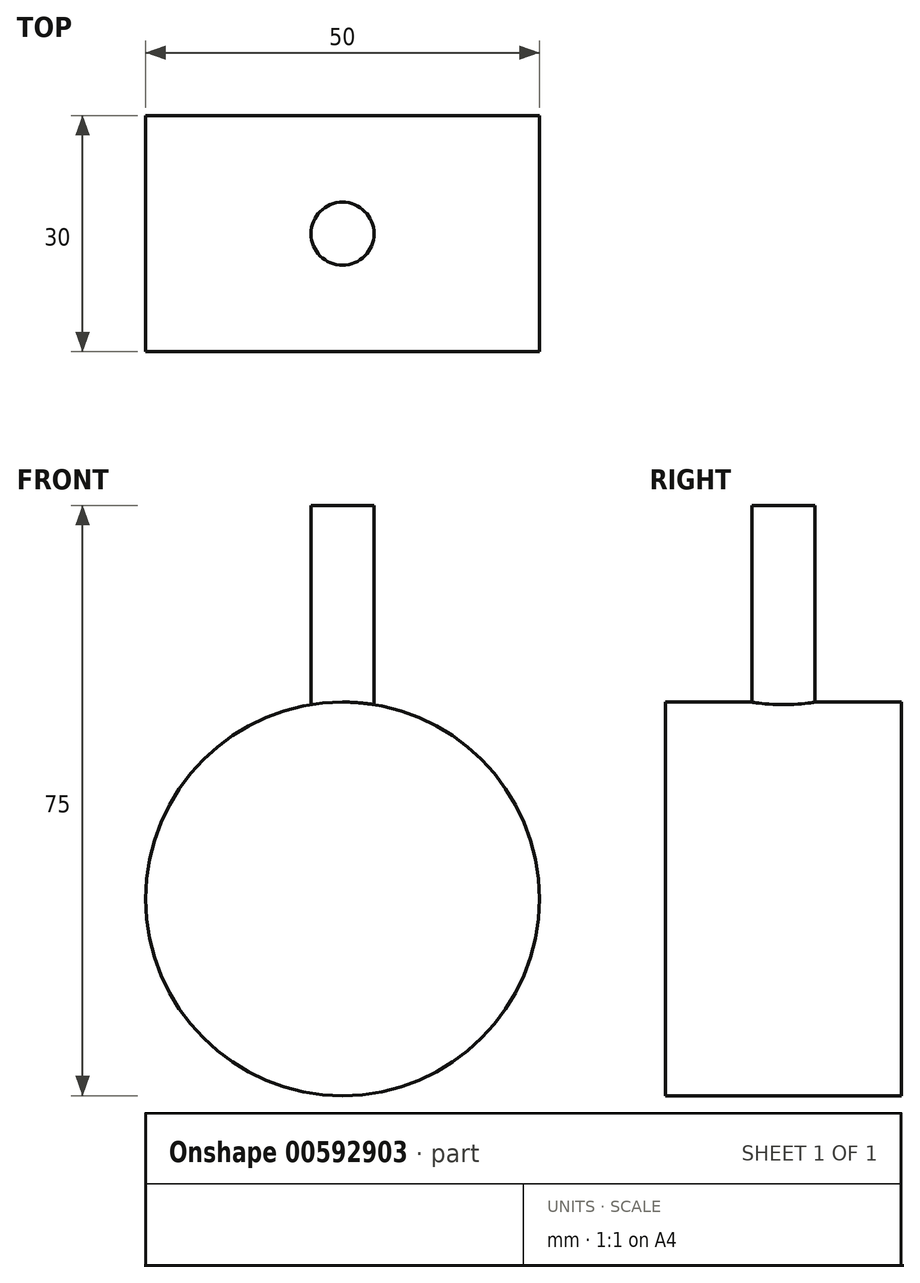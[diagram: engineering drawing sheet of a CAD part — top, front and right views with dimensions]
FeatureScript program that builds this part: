
annotation { "Feature Type Name" : "Feature", "Feature Type Description" : "" }
export const myFeature = defineFeature(function(context is Context, id is Id, definition is map)
    precondition{}
    {
        {
            var Q0;
            Q0=qCreatedBy(makeId("Front.planeOp"),FACE);
            var sketch = newSketch(context, id + "F0", { "sketchPlane" : qUnion([Q0])});
            skCircle(sketch, "E0", {"center": v(0, 0) * mm, "radius": 25 * mm});
            skSolve(sketch);
        }
        {
            var Q0;
            Q0=qCreatedBy(makeId("Top.planeOp"),FACE);
            var sketch = newSketch(context, id + "F1", { "sketchPlane" : qUnion([Q0])});
            skCircle(sketch, "E1", {"center": v(0, 0) * mm, "radius": 4 * mm});
            skSolve(sketch);
        }
        {
            var Q0;
            Q0 = qSketchRegion(id + "F0", true);
            extrude(context, id + "F2", {"entities" : qUnion([Q0]), "depth" : 15 * mm, "offsetDistance" : 25 * mm, "hasSecondDirection" : true, "secondDirectionOppositeDirection" : true, "secondDirectionDepth" : 15 * mm});
        }
        {
            var Q0;
            Q0 = qSketchRegion(id + "F1", true);
            extrude(context, id + "F3", {"entities" : qUnion([Q0]), "operationType" : NewBodyOperationType.ADD, "depth" : 50 * mm, "offsetDistance" : 25 * mm});
        }
    });
